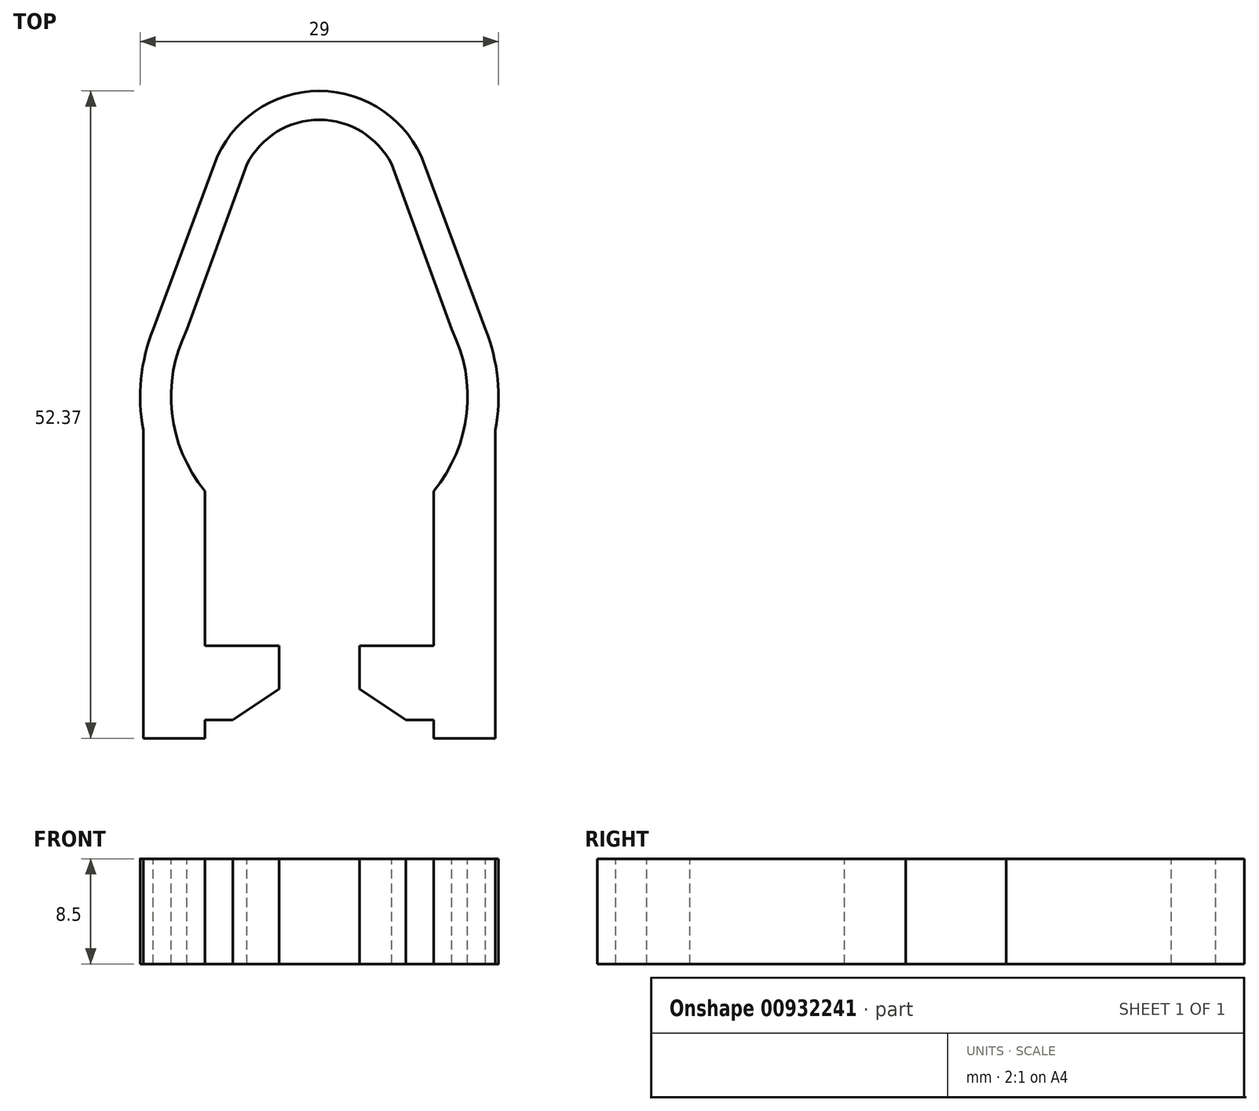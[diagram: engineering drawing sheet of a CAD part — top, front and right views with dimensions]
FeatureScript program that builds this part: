
annotation { "Feature Type Name" : "Feature", "Feature Type Description" : "" }
export const myFeature = defineFeature(function(context is Context, id is Id, definition is map)
    precondition{}
    {
        {
            var Q0;
            Q0=qCreatedBy(makeId("Top.planeOp"),FACE);
            var sketch = newSketch(context, id + "F0", { "sketchPlane" : qUnion([Q0])});
            skPoint(sketch, "E0", {"position": v(0, 0) * mm});
            skPoint(sketch, "E1", {"position": v(-12, 0) * mm});
            skPoint(sketch, "E2", {"position": v(12, 0) * mm});
            skArc(sketch, "E3", {"start": v(-11.67, 2.79) * mm, "mid": v(-11.69, -2.71) * mm, "end": v(-9.25, -7.64) * mm});
            skPoint(sketch, "E4", {"position": v(-10.7, 5.42) * mm});
            skPoint(sketch, "E5", {"position": v(10.7, 5.42) * mm});
            skLineSegment(sketch, "E6", {"start": v(-11.67, 2.79) * mm, "end": v(-11.35, 2.71) * mm, "construction": true});
            skLineSegment(sketch, "E7", {"start": v(11.35, 2.71) * mm, "end": v(11.67, 2.79) * mm, "construction": true});
            skPoint(sketch, "E8", {"position": v(0, -12) * mm});
            skPoint(sketch, "E9", {"position": v(-14.5, 0) * mm});
            skPoint(sketch, "E10", {"position": v(14.5, 0) * mm});
            skArc(sketch, "E11", {"start": v(-14.1, 3.37) * mm, "mid": v(-14.4, 1.7) * mm, "end": v(-14.5, 0) * mm});
            skLineSegment(sketch, "E12", {"start": v(-14.1, 3.37) * mm, "end": v(-13.72, 3.28) * mm, "construction": true});
            skLineSegment(sketch, "E13", {"start": v(13.72, 3.28) * mm, "end": v(14.1, 3.37) * mm, "construction": true});
            skLineSegment(sketch, "E14", {"start": v(-14.5, 0) * mm, "end": v(0, 0) * mm, "construction": true});
            skPoint(sketch, "E15", {"position": v(-9.25, -11.17) * mm});
            skPoint(sketch, "E16", {"position": v(9.25, -11.17) * mm});
            skLineSegment(sketch, "E17", {"start": v(-9.25, -11.17) * mm, "end": v(9.25, -11.17) * mm, "construction": true});
            skLineSegment(sketch, "E18", {"start": v(-9.25, -11.17) * mm, "end": v(-9.25, -20.14) * mm});
            skLineSegment(sketch, "E19", {"start": v(9.25, -11.17) * mm, "end": v(9.25, -20.14) * mm});
            skPoint(sketch, "E20", {"position": v(-14.25, -2.68) * mm});
            skPoint(sketch, "E21", {"position": v(14.25, -2.68) * mm});
            skLineSegment(sketch, "E22", {"start": v(-14.25, -2.68) * mm, "end": v(14.25, -2.68) * mm, "construction": true});
            skLineSegment(sketch, "E23", {"start": v(-14.25, -2.68) * mm, "end": v(-14.25, -21.14) * mm});
            skLineSegment(sketch, "E24", {"start": v(14.25, -2.68) * mm, "end": v(14.25, -21.43) * mm});
            skLineSegment(sketch, "E25", {"start": v(-3.25, -21.14) * mm, "end": v(-3.25, -23.64) * mm});
            skLineSegment(sketch, "E26", {"start": v(-3.25, -23.64) * mm, "end": v(-7, -26.14) * mm});
            skLineSegment(sketch, "E27", {"start": v(-9.25, -27.64) * mm, "end": v(-14.25, -27.64) * mm});
            skLineSegment(sketch, "E28", {"start": v(-14.25, -27.64) * mm, "end": v(-14.25, -21.14) * mm});
            skLineSegment(sketch, "E29", {"start": v(3.25, -21.14) * mm, "end": v(3.25, -23.64) * mm});
            skLineSegment(sketch, "E30", {"start": v(3.25, -23.64) * mm, "end": v(7, -26.14) * mm});
            skLineSegment(sketch, "E31", {"start": v(9.25, -27.64) * mm, "end": v(14.25, -27.64) * mm});
            skLineSegment(sketch, "E32", {"start": v(14.25, -27.64) * mm, "end": v(14.25, -21.43) * mm});
            skLineSegment(sketch, "E33", {"start": v(-14.25, -11.17) * mm, "end": v(-9.25, -11.17) * mm, "construction": true});
            skLineSegment(sketch, "E34", {"start": v(9.25, -11.17) * mm, "end": v(14.25, -11.17) * mm, "construction": true});
            skLineSegment(sketch, "E35", {"start": v(-9.25, -11.17) * mm, "end": v(-9.25, -7.64) * mm});
            skLineSegment(sketch, "E36", {"start": v(9.25, -11.17) * mm, "end": v(9.25, -7.64) * mm});
            skArc(sketch, "E37.trimOffspring", {"start": v(9.25, -7.64) * mm, "mid": v(11.69, -2.71) * mm, "end": v(11.67, 2.79) * mm});
            skArc(sketch, "E38.trimOffspring", {"start": v(14.5, 0) * mm, "mid": v(14.4, 1.7) * mm, "end": v(14.1, 3.37) * mm});
            skArc(sketch, "E39", {"start": v(14.25, -2.68) * mm, "mid": v(14.44, -1.35) * mm, "end": v(14.5, 0) * mm});
            skArc(sketch, "E40.trimOffspring", {"start": v(-14.1, 3.37) * mm, "mid": v(-14.5, 0.35) * mm, "end": v(-14.25, -2.68) * mm});
            skArc(sketch, "E41", {"start": v(9.25, -7.64) * mm, "mid": v(11.93, -1.33) * mm, "end": v(10.7, 5.42) * mm});
            skLineSegment(sketch, "E42", {"start": v(-10.7, 5.42) * mm, "end": v(-5.85, 18.8) * mm});
            skLineSegment(sketch, "E43", {"start": v(10.7, 5.42) * mm, "end": v(5.85, 18.8) * mm});
            skArc(sketch, "E44.trimOffspring", {"start": v(-10.7, 5.42) * mm, "mid": v(-11.93, -1.33) * mm, "end": v(-9.25, -7.64) * mm});
            skLineSegment(sketch, "E45", {"start": v(-9.25, -20.14) * mm, "end": v(-3.25, -20.14) * mm});
            skLineSegment(sketch, "E46", {"start": v(-3.25, -21.14) * mm, "end": v(-3.25, -20.14) * mm});
            skLineSegment(sketch, "E47", {"start": v(9.25, -20.14) * mm, "end": v(3.25, -20.14) * mm});
            skLineSegment(sketch, "E48", {"start": v(3.25, -20.14) * mm, "end": v(3.25, -21.14) * mm});
            skPoint(sketch, "E49.orphan", {"position": v(-9.25, -21.14) * mm});
            skPoint(sketch, "E50.orphan", {"position": v(9.25, -21.43) * mm});
            skLineSegment(sketch, "E51", {"start": v(9.25, -27.64) * mm, "end": v(9.25, -26.14) * mm});
            skLineSegment(sketch, "E52", {"start": v(9.25, -26.14) * mm, "end": v(7, -26.14) * mm});
            skLineSegment(sketch, "E53", {"start": v(-9.25, -27.64) * mm, "end": v(-9.25, -26.14) * mm});
            skLineSegment(sketch, "E54", {"start": v(-9.25, -26.14) * mm, "end": v(-7, -26.14) * mm});
            skArc(sketch, "E55", {"start": v(5.85, 18.8) * mm, "mid": v(0, 22.4) * mm, "end": v(-5.85, 18.8) * mm});
            skPoint(sketch, "E56", {"position": v(0, 22.4) * mm});
            skLineSegment(sketch, "E57", {"start": v(-8.5, 18.8) * mm, "end": v(-5.85, 18.8) * mm, "construction": true});
            skLineSegment(sketch, "E58", {"start": v(5.85, 18.8) * mm, "end": v(8.5, 18.8) * mm, "construction": true});
            skLineSegment(sketch, "E59", {"start": v(-13.36, 5.42) * mm, "end": v(-10.7, 5.42) * mm, "construction": true});
            skLineSegment(sketch, "E60", {"start": v(13.36, 5.42) * mm, "end": v(10.7, 5.42) * mm, "construction": true});
            skArc(sketch, "E61", {"start": v(-13.44, 5.45) * mm, "mid": v(-14.43, 1.44) * mm, "end": v(-14.25, -2.68) * mm});
            skCircle(sketch, "E62", {"center": v(0, 0) * mm, "radius": 12 * mm, "construction": true});
            skArc(sketch, "E63.trimOffspring", {"start": v(14.25, -2.68) * mm, "mid": v(14.43, 1.44) * mm, "end": v(13.44, 5.45) * mm});
            skLineSegment(sketch, "E64", {"start": v(-13.44, 5.45) * mm, "end": v(-8.5, 18.8) * mm});
            skLineSegment(sketch, "E65", {"start": v(13.44, 5.45) * mm, "end": v(8.5, 18.8) * mm});
            skArc(sketch, "E66", {"start": v(8.5, 18.8) * mm, "mid": v(0, 24.73) * mm, "end": v(-8.5, 18.8) * mm});
            skLineSegment(sketch, "E67", {"start": v(0, 24.73) * mm, "end": v(0, -12) * mm, "construction": true});
            skLineSegment(sketch, "E68", {"start": v(-8.5, 18.8) * mm, "end": v(8.5, 18.8) * mm, "construction": true});
            skPoint(sketch, "E69", {"position": v(0, 18.8) * mm});
            skSolve(sketch);
        }
        {
            var Q0;
            Q0=qSketchRegion(id+"F0",true);
            var Q1;
            Q1=makeQuery(id+"F0.imprint","IMPRINT",FACE,{"disambiguationData":[TD([[makeQuery(id+"F0.imprint","IMPRINT",EDGE,{"derivedFrom":sQuery(id+"F0.wireOp",EDGE,"f92893d9-89b3-415d-a26c-5dc1b98e07fd.sketch_text.stroke-0")}),-1.0]])]});
            extrude(context, id + "F1", {"entities" : qUnion([Q0, Q1]), "oppositeDirection" : true, "depth" : 8.5 * mm, "offsetDistance" : 25 * mm});
        }
    });
